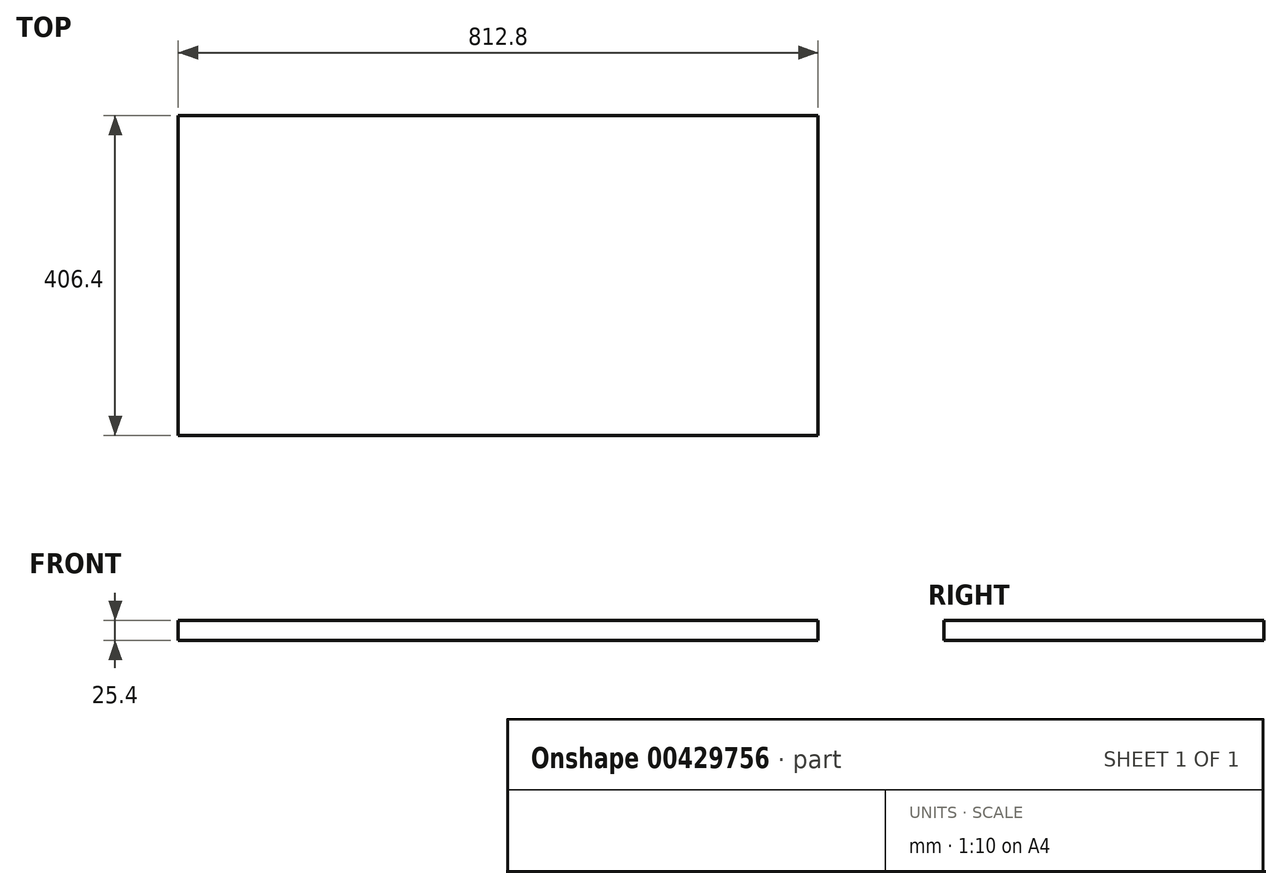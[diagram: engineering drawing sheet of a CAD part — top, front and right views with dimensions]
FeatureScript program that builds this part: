
annotation { "Feature Type Name" : "Feature", "Feature Type Description" : "" }
export const myFeature = defineFeature(function(context is Context, id is Id, definition is map)
    precondition{}
    {
        {
            var Q0;
            Q0=qCreatedBy(makeId("Top.planeOp"),FACE);
            var sketch = newSketch(context, id + "F0", { "sketchPlane" : qUnion([Q0])});
            skLineSegment(sketch, "E0.bottom", {"start": v(-406.4, -406.4) * mm, "end": v(406.4, -406.4) * mm});
            skLineSegment(sketch, "E0.top", {"start": v(-406.4, 406.4) * mm, "end": v(406.4, 406.4) * mm});
            skLineSegment(sketch, "E0.left", {"start": v(-406.4, -406.4) * mm, "end": v(-406.4, 406.4) * mm});
            skLineSegment(sketch, "E0.right", {"start": v(406.4, -406.4) * mm, "end": v(406.4, 406.4) * mm});
            skSolve(sketch);
        }
        {
            var Q0;
            Q0 = qSketchRegion(id + "F0", true);
            extrude(context, id + "F1", {"entities" : qUnion([Q0]), "depth" : 25.4 * mm});
        }
        {
            var Q0;
            Q0=makeQuery(id+"F1.opExtrude","CAP_FACE",FACE,{"disambiguationData":[OSD([sQuery(id+"F0.wireOp",EDGE,"E0.bottom"),sQuery(id+"F0.wireOp",EDGE,"E0.top"),sQuery(id+"F0.wireOp",EDGE,"E0.left"),sQuery(id+"F0.wireOp",EDGE,"E0.right")])],"isStart":false});
            var sketch = newSketch(context, id + "F2", { "sketchPlane" : qUnion([Q0])});
            skLineSegment(sketch, "E1", {"start": v(406.4, 406.4) * mm, "end": v(406.4, 401.9) * mm});
            skLineSegment(sketch, "E2", {"start": v(-401.9, -406.4) * mm, "end": v(-406.4, -406.4) * mm});
            skLineSegment(sketch, "E3", {"start": v(-406.4, 406.4) * mm, "end": v(406.4, 406.4) * mm});
            skPoint(sketch, "E4", {"position": v(0, 0) * mm});
            skLineSegment(sketch, "E5", {"start": v(-406.4, 0) * mm, "end": v(406.4, 0) * mm});
            skLineSegment(sketch, "E6", {"start": v(406.4, 0) * mm, "end": v(406.4, 406.4) * mm});
            skLineSegment(sketch, "E7", {"start": v(-406.4, 0) * mm, "end": v(-406.4, 406.4) * mm});
            skSolve(sketch);
        }
        {
            var Q0;
            Q0 = qSketchRegion(id + "F2", true);
            extrude(context, id + "F3", {"entities" : qUnion([Q0]), "operationType" : NewBodyOperationType.REMOVE, "endBound" : BoundingType.THROUGH_ALL, "oppositeDirection" : true, "depth" : 25.4 * mm});
        }
    });
